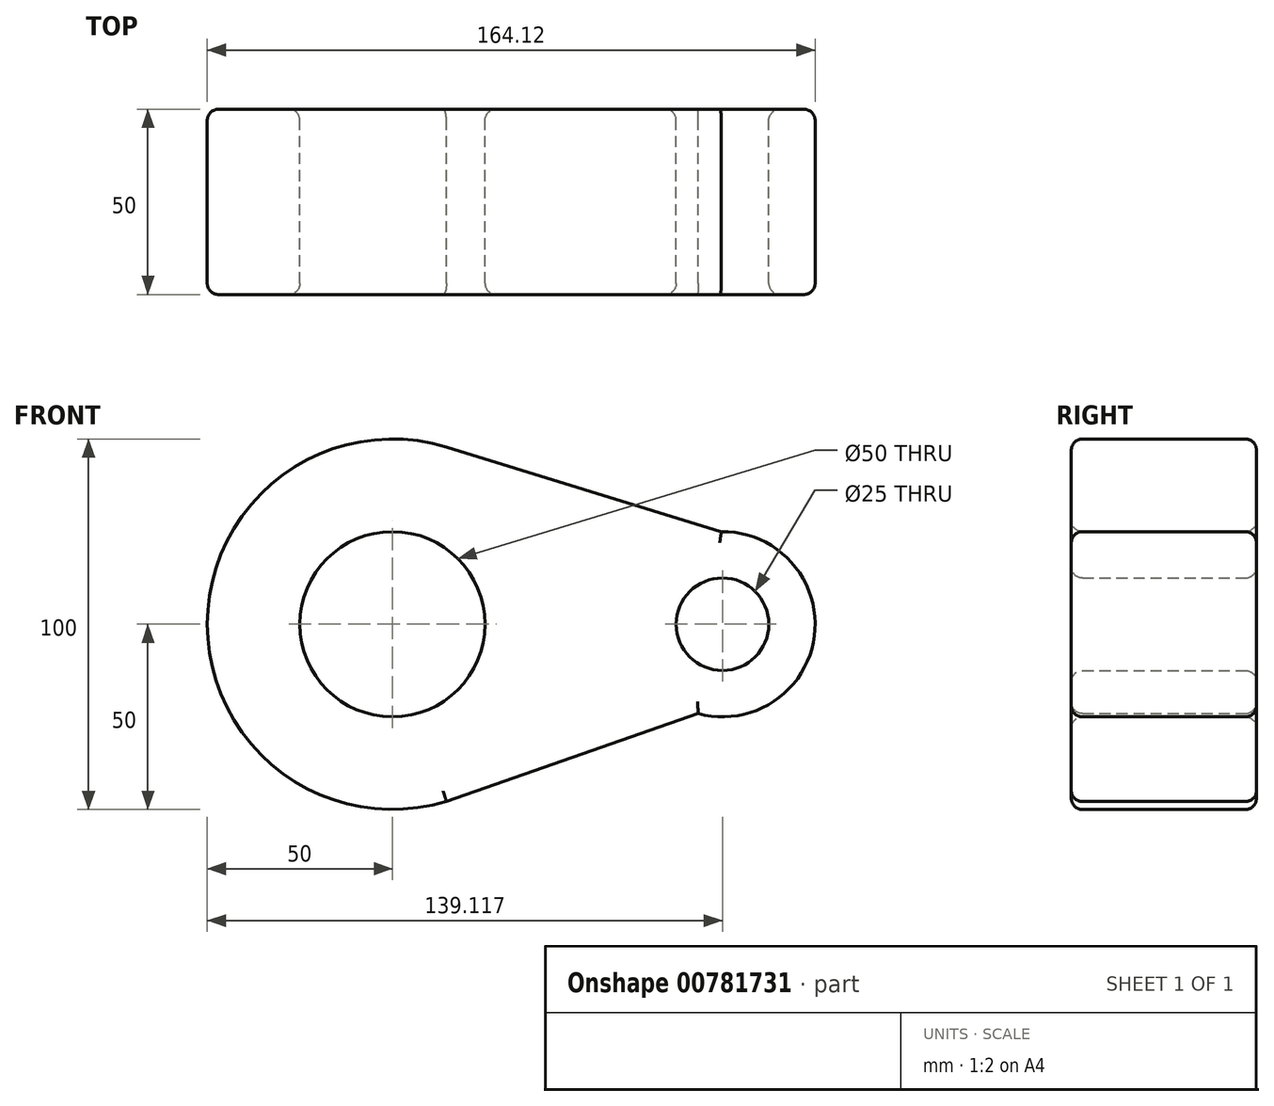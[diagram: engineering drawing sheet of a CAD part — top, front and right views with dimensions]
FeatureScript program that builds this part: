
annotation { "Feature Type Name" : "Feature", "Feature Type Description" : "" }
export const myFeature = defineFeature(function(context is Context, id is Id, definition is map)
    precondition{}
    {
        {
            var Q0;
            Q0=qCreatedBy(makeId("Front.planeOp"),FACE);
            var sketch = newSketch(context, id + "F0", { "sketchPlane" : qUnion([Q0])});
            skArc(sketch, "E0", {"start": v(14.58, 47.83) * mm, "mid": v(-50, 0) * mm, "end": v(14.58, -47.83) * mm});
            skArc(sketch, "E1", {"start": v(82.51, -24.11) * mm, "mid": v(113.92, -3.17) * mm, "end": v(88.79, 25) * mm});
            skLineSegment(sketch, "E2", {"start": v(14.58, -47.83) * mm, "end": v(82.51, -24.11) * mm});
            skLineSegment(sketch, "E3", {"start": v(88.79, 25) * mm, "end": v(14.58, 47.83) * mm});
            skCircle(sketch, "E4", {"center": v(0, 0) * mm, "radius": 25 * mm});
            skCircle(sketch, "E5", {"center": v(89.12, 0) * mm, "radius": 12.5 * mm});
            skSolve(sketch);
        }
        {
            var Q0;
            Q0=makeQuery(id+"F0.imprint","IMPRINT",FACE,{"disambiguationData":[TD([[makeQuery(id+"F0.imprint","IMPRINT",EDGE,{"derivedFrom":sQuery(id+"F0.wireOp",EDGE,"E0")}),1.0]])]});
            extrude(context, id + "F1", {"entities" : qUnion([Q0]), "depth" : 50 * mm, "offsetDistance" : 25 * mm});
        }
        {
            var Q0;
            Q0=makeQuery(id+"F1.opExtrude","CAP_EDGE",EDGE,{"disambiguationData":[OSD([sQuery(id+"F0.wireOp",EDGE,"E4")])],"isStart":false});
            var Q1;
            Q1=makeQuery(id+"F1.opExtrude","CAP_EDGE",EDGE,{"disambiguationData":[OSD([sQuery(id+"F0.wireOp",EDGE,"E5")])],"isStart":true});
            var Q2;
            Q2=makeQuery(id+"F1.opExtrude","CAP_EDGE",EDGE,{"disambiguationData":[OSD([sQuery(id+"F0.wireOp",EDGE,"E4")])],"isStart":true});
            var Q3;
            Q3=makeQuery(id+"F1.opExtrude","CAP_EDGE",EDGE,{"disambiguationData":[OSD([sQuery(id+"F0.wireOp",EDGE,"E5")])],"isStart":false});
            var Q4;
            Q4=makeQuery(id+"F1.opExtrude","CAP_EDGE",EDGE,{"disambiguationData":[OSD([sQuery(id+"F0.wireOp",EDGE,"E0")])],"isStart":false});
            var Q5;
            Q5=makeQuery(id+"F1.opExtrude","CAP_EDGE",EDGE,{"disambiguationData":[OSD([sQuery(id+"F0.wireOp",EDGE,"E3")])],"isStart":false});
            var Q6;
            Q6=makeQuery(id+"F1.opExtrude","CAP_EDGE",EDGE,{"disambiguationData":[OSD([sQuery(id+"F0.wireOp",EDGE,"E1")])],"isStart":false});
            var Q7;
            Q7=makeQuery(id+"F1.opExtrude","CAP_EDGE",EDGE,{"disambiguationData":[OSD([sQuery(id+"F0.wireOp",EDGE,"E2")])],"isStart":false});
            var Q8;
            Q8=makeQuery(id+"F1.opExtrude","CAP_EDGE",EDGE,{"disambiguationData":[OSD([sQuery(id+"F0.wireOp",EDGE,"E2")])],"isStart":true});
            var Q9;
            Q9=makeQuery(id+"F1.opExtrude","CAP_EDGE",EDGE,{"disambiguationData":[OSD([sQuery(id+"F0.wireOp",EDGE,"E1")])],"isStart":true});
            var Q10;
            Q10=makeQuery(id+"F1.opExtrude","CAP_EDGE",EDGE,{"disambiguationData":[OSD([sQuery(id+"F0.wireOp",EDGE,"E3")])],"isStart":true});
            var Q11;
            Q11=makeQuery(id+"F1.opExtrude","CAP_EDGE",EDGE,{"disambiguationData":[OSD([sQuery(id+"F0.wireOp",EDGE,"E0")])],"isStart":true});
            fillet(context, id + "F2", {"entities" : qUnion([Q0, Q1, Q2, Q3, Q4, Q5, Q6, Q7, Q8, Q9, Q10, Q11]), "radius" : 3 * mm, "tangentPropagation" : true, "allowEdgeOverflow" : false});
        }
    });
